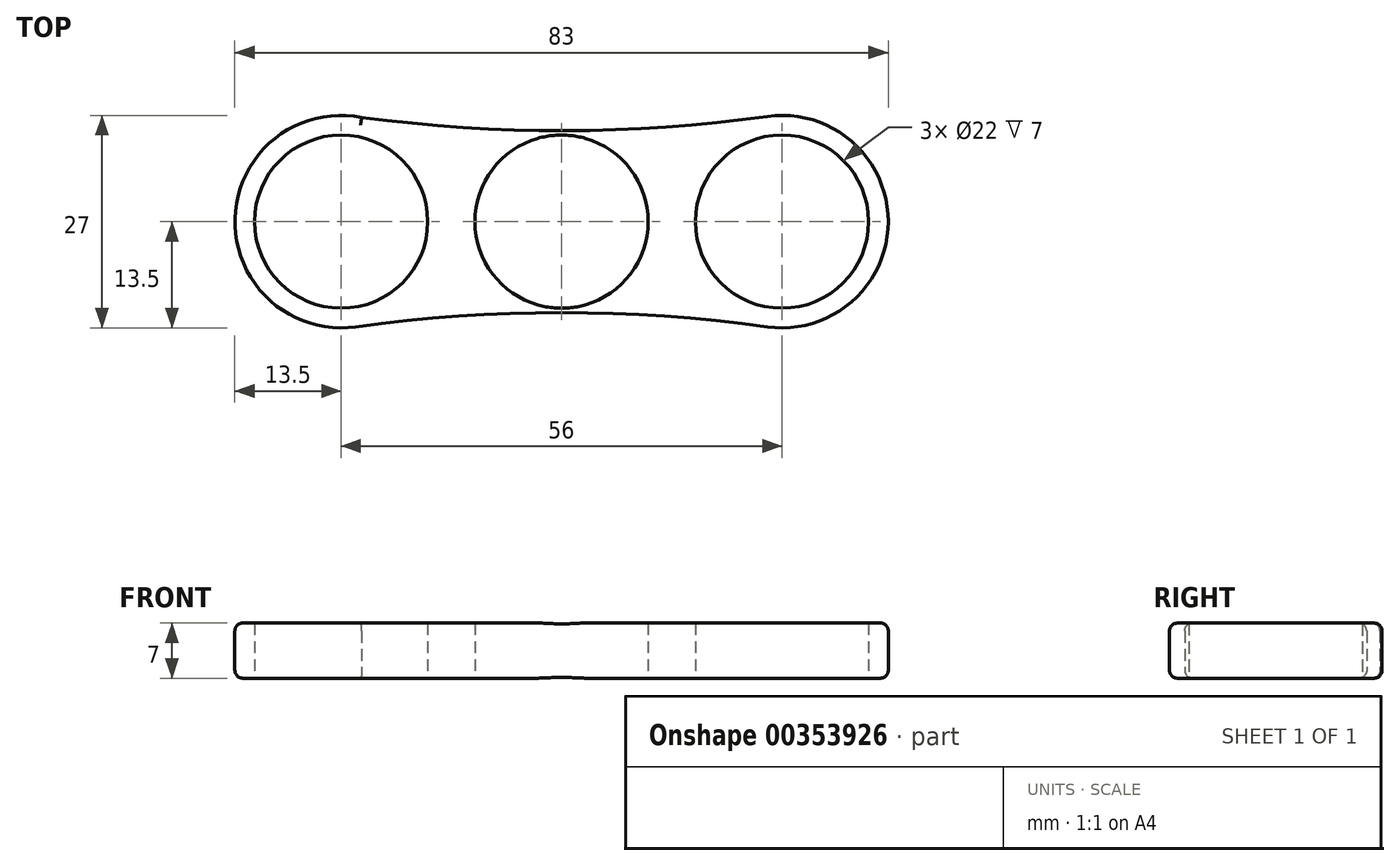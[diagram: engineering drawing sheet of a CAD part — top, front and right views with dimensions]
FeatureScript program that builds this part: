
annotation { "Feature Type Name" : "Feature", "Feature Type Description" : "" }
export const myFeature = defineFeature(function(context is Context, id is Id, definition is map)
    precondition{}
    {
        {
            var Q0;
            Q0=qCreatedBy(makeId("Top.planeOp"),FACE);
            var sketch = newSketch(context, id + "F0", { "sketchPlane" : qUnion([Q0])});
            skCircle(sketch, "E0", {"center": v(-28, 0) * mm, "radius": 11 * mm});
            skCircle(sketch, "E1", {"center": v(28, 0) * mm, "radius": 11 * mm});
            skCircle(sketch, "E2", {"center": v(-28, 0) * mm, "radius": 13.5 * mm});
            skCircle(sketch, "E3", {"center": v(28, 0) * mm, "radius": 13.5 * mm});
            skPoint(sketch, "E4.middle", {"position": v(0, 0) * mm});
            skCircle(sketch, "E5", {"center": v(0, 0) * mm, "radius": 11 * mm});
            skArc(sketch, "E6", {"start": v(26.14, -13.37) * mm, "mid": v(0, -11.56) * mm, "end": v(-26.14, -13.37) * mm});
            skArc(sketch, "E7", {"start": v(-25.37, 13.24) * mm, "mid": v(0.39, 11.55) * mm, "end": v(26.14, 13.37) * mm});
            skSolve(sketch);
        }
        {
            var Q0;
            {var subQ0=sQuery(id+"F0.wireOp",EDGE,"2qMNczL3-bLPZ-TAMb-2hCG-JQhvqwVsmHuA");var subQ1=sQuery(id+"F0.wireOp",EDGE,"E2");var subQ2=makeQuery(id+"F0.imprint","INTERSECT",VERTEX,{"disambiguationData":[OD(0.0)],"derivedFrom":[subQ1,subQ0]});Q0=makeQuery(id+"F0.imprint","IMPRINT",FACE,{"disambiguationData":[TD([[makeQuery(id+"F0.imprint","IMPRINT",EDGE,{"disambiguationData":[TD([[subQ2,1.0]])],"derivedFrom":subQ1}),1.0]])]});}
            var Q1;
            {var subQ0=sQuery(id+"F0.wireOp",EDGE,"Zn8wSCEo-pRYU-YKty-iMrf-FbREp7J4IGsd");var subQ1=sQuery(id+"F0.wireOp",EDGE,"E2");var subQ2=makeQuery(id+"F0.imprint","INTERSECT",VERTEX,{"disambiguationData":[OD(0.0)],"derivedFrom":[subQ1,subQ0]});Q1=makeQuery(id+"F0.imprint","IMPRINT",FACE,{"disambiguationData":[TD([[makeQuery(id+"F0.imprint","IMPRINT",EDGE,{"disambiguationData":[TD([[subQ2,-1.0]])],"derivedFrom":subQ1}),1.0]])]});}
            var Q2;
            {var subQ0=sQuery(id+"F0.wireOp",EDGE,"2qMNczL3-bLPZ-TAMb-2hCG-JQhvqwVsmHuA");var subQ1=sQuery(id+"F0.wireOp",EDGE,"E3");var subQ2=makeQuery(id+"F0.imprint","INTERSECT",VERTEX,{"disambiguationData":[OD(0.0)],"derivedFrom":[subQ1,subQ0]});Q2=makeQuery(id+"F0.imprint","IMPRINT",FACE,{"disambiguationData":[TD([[makeQuery(id+"F0.imprint","IMPRINT",EDGE,{"disambiguationData":[TD([[subQ2,-1.0]])],"derivedFrom":subQ1}),1.0]])]});}
            var Q3;
            {var subQ0=sQuery(id+"F0.wireOp",EDGE,"Zn8wSCEo-pRYU-YKty-iMrf-FbREp7J4IGsd");var subQ1=sQuery(id+"F0.wireOp",EDGE,"E3");var subQ2=makeQuery(id+"F0.imprint","INTERSECT",VERTEX,{"disambiguationData":[OD(0.0)],"derivedFrom":[subQ1,subQ0]});Q3=makeQuery(id+"F0.imprint","IMPRINT",FACE,{"disambiguationData":[TD([[makeQuery(id+"F0.imprint","IMPRINT",EDGE,{"disambiguationData":[TD([[subQ2,1.0]])],"derivedFrom":subQ1}),1.0]])]});}
            var Q4;
            Q4=makeQuery(id+"F0.imprint","IMPRINT",FACE,{"disambiguationData":[TD([[makeQuery(id+"F0.imprint","IMPRINT",EDGE,{"derivedFrom":sQuery(id+"F0.wireOp",EDGE,"E0")}),-1.0]])]});
            var Q5;
            Q5=makeQuery(id+"F0.imprint","IMPRINT",FACE,{"disambiguationData":[TD([[makeQuery(id+"F0.imprint","IMPRINT",EDGE,{"derivedFrom":sQuery(id+"F0.wireOp",EDGE,"E1")}),-1.0]])]});
            var Q6;
            Q6=makeQuery(id+"F0.imprint","IMPRINT",FACE,{"disambiguationData":[TD([[makeQuery(id+"F0.imprint","IMPRINT",EDGE,{"derivedFrom":sQuery(id+"F0.wireOp",EDGE,"E5")}),-1.0]])]});
            extrude(context, id + "F1", {"entities" : qUnion([Q0, Q1, Q2, Q3, Q4, Q5, Q6]), "endBound" : BoundingType.SYMMETRIC, "depth" : 7 * mm});
        }
        {
            var Q0;
            Q0=makeQuery(id+"F1.opExtrude","CAP_EDGE",EDGE,{"disambiguationData":[OSD([sQuery(id+"F0.wireOp",EDGE,"E3")])],"isStart":true});
            var Q1;
            Q1=makeQuery(id+"F1.opExtrude","CAP_EDGE",EDGE,{"disambiguationData":[OSD([sQuery(id+"F0.wireOp",EDGE,"2qMNczL3-bLPZ-TAMb-2hCG-JQhvqwVsmHuA")])],"isStart":true});
            var Q2;
            Q2=makeQuery(id+"F1.opExtrude","CAP_EDGE",EDGE,{"disambiguationData":[OSD([sQuery(id+"F0.wireOp",EDGE,"E2")])],"isStart":true});
            var Q3;
            Q3=makeQuery(id+"F1.opExtrude","CAP_EDGE",EDGE,{"disambiguationData":[OSD([sQuery(id+"F0.wireOp",EDGE,"Zn8wSCEo-pRYU-YKty-iMrf-FbREp7J4IGsd")])],"isStart":true});
            var Q4;
            Q4=makeQuery(id+"F1.opExtrude","CAP_EDGE",EDGE,{"disambiguationData":[OSD([sQuery(id+"F0.wireOp",EDGE,"E3")])],"isStart":false});
            var Q5;
            Q5=makeQuery(id+"F1.opExtrude","CAP_EDGE",EDGE,{"disambiguationData":[OSD([sQuery(id+"F0.wireOp",EDGE,"Zn8wSCEo-pRYU-YKty-iMrf-FbREp7J4IGsd")])],"isStart":false});
            var Q6;
            Q6=makeQuery(id+"F1.opExtrude","CAP_EDGE",EDGE,{"disambiguationData":[OSD([sQuery(id+"F0.wireOp",EDGE,"2qMNczL3-bLPZ-TAMb-2hCG-JQhvqwVsmHuA")])],"isStart":false});
            var Q7;
            Q7=makeQuery(id+"F1.opExtrude","CAP_EDGE",EDGE,{"disambiguationData":[OSD([sQuery(id+"F0.wireOp",EDGE,"E2")])],"isStart":false});
            fillet(context, id + "F2", {"entities" : qUnion([Q0, Q1, Q2, Q3, Q4, Q5, Q6, Q7]), "radius" : 1 * mm, "tangentPropagation" : true, "allowEdgeOverflow" : false});
        }
    });
